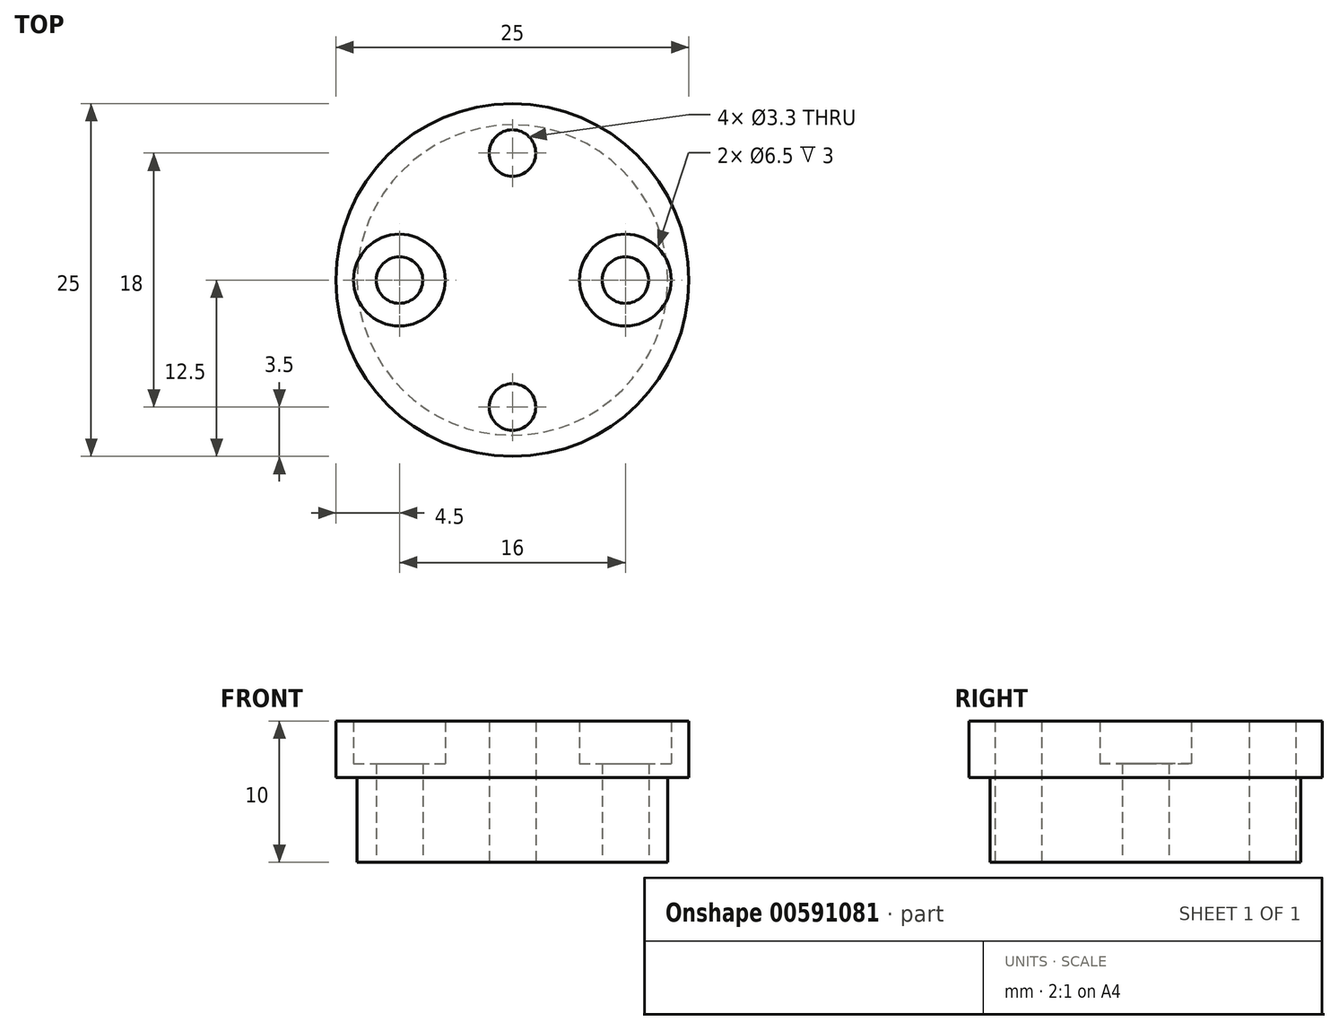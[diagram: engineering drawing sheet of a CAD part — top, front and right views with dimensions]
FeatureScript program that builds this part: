
annotation { "Feature Type Name" : "Feature", "Feature Type Description" : "" }
export const myFeature = defineFeature(function(context is Context, id is Id, definition is map)
    precondition{}
    {
        {
            var Q0;
            Q0=qCreatedBy(makeId("Front.planeOp"),FACE);
            var sketch = newSketch(context, id + "F0", { "sketchPlane" : qUnion([Q0])});
            skLineSegment(sketch, "E0", {"start": v(0, 0) * mm, "end": v(11, 0) * mm});
            skLineSegment(sketch, "E1", {"start": v(11, 0) * mm, "end": v(11, 6) * mm});
            skLineSegment(sketch, "E2", {"start": v(11, 6) * mm, "end": v(12.5, 6) * mm});
            skLineSegment(sketch, "E3", {"start": v(14, 10) * mm, "end": v(0, 10) * mm});
            skLineSegment(sketch, "E4", {"start": v(0, 10) * mm, "end": v(0, 0) * mm});
            skLineSegment(sketch, "E5", {"start": v(14, 10) * mm, "end": v(11, 0) * mm});
            skLineSegment(sketch, "E6", {"start": v(12.5, 10) * mm, "end": v(12.5, 6) * mm});
            skSolve(sketch);
        }
        {
            var Q0;
            Q0=makeQuery(id+"F0.imprint","IMPRINT",FACE,{"disambiguationData":[TD([[makeQuery(id+"F0.imprint","IMPRINT",EDGE,{"derivedFrom":sQuery(id+"F0.wireOp",EDGE,"E0")}),1.0]])]});
            var Q1;
            Q1=sQuery(id+"F0.wireOp",EDGE,"E4");
            revolve(context, id + "F1", {"entities" : qUnion([Q0]), "axis" : qUnion([Q1]), "revolveType" : RevolveType.FULL});
        }
        {
            var Q0;
            Q0=makeQuery(id+"F1.opRevolve","SWEPT_FACE",FACE,{"disambiguationData":[OSD([sQuery(id+"F0.wireOp",EDGE,"E3")])]});
            var sketch = newSketch(context, id + "F2", { "sketchPlane" : qUnion([Q0])});
            skLineSegment(sketch, "E7", {"start": v(-8, 0) * mm, "end": v(8, 0) * mm});
            skLineSegment(sketch, "E8", {"start": v(0, 9) * mm, "end": v(0, -9) * mm});
            skCircle(sketch, "E9.0", {"center": v(0, 0) * mm, "radius": 12.5 * mm});
            skSolve(sketch);
        }
        {
            var Q0;
            Q0=sQuery(id+"F2.wireOp",VERTEX,"E8.start");
            var Q1;
            Q1=sQuery(id+"F2.wireOp",VERTEX,"E8.end");
            var Q2;
            Q2=makeQuery(id+"F1.opRevolve","SWEPT_BODY",BODY,{"disambiguationData":[OSD([sQuery(id+"F0.wireOp",EDGE,"E0"),sQuery(id+"F0.wireOp",EDGE,"E1"),sQuery(id+"F0.wireOp",EDGE,"E2"),sQuery(id+"F0.wireOp",EDGE,"E3"),sQuery(id+"F0.wireOp",EDGE,"E4"),sQuery(id+"F0.wireOp",EDGE,"E6")])]});
            hole(context, id + "F3", {"style" : HoleStyle.SIMPLE, "endStyle" : HoleEndStyle.BLIND, "standardTappedOrClearance" : lookupTablePath({ "standard" : "ISO", "fit" : "Normal", "size" : "M3", "type" : "Clearance" }), "standardBlindInLast" : lookupTablePath({ "fit" : "Standard", "standard" : "ISO", "size" : "M3", "type" : "Clearance" }), "holeDiameter" : 3.3 * mm, "majorDiameter" : 5 * mm, "holeDepth" : 10 * mm, "isTappedThrough" : true, "tappedDepth" : 12 * mm, "tapClearance" : 3, "locations" : qUnion([Q0, Q1]), "scope" : qUnion([Q2])});
        }
        {
            var Q0;
            Q0=sQuery(id+"F2.wireOp",VERTEX,"E7.start");
            var Q1;
            Q1=sQuery(id+"F2.wireOp",VERTEX,"E7.end");
            var Q2;
            Q2=makeQuery(id+"F1.opRevolve","SWEPT_BODY",BODY,{"disambiguationData":[OSD([sQuery(id+"F0.wireOp",EDGE,"E0"),sQuery(id+"F0.wireOp",EDGE,"E1"),sQuery(id+"F0.wireOp",EDGE,"E2"),sQuery(id+"F0.wireOp",EDGE,"E3"),sQuery(id+"F0.wireOp",EDGE,"E4"),sQuery(id+"F0.wireOp",EDGE,"E6")])]});
            hole(context, id + "F4", {"style" : HoleStyle.C_BORE, "endStyle" : HoleEndStyle.BLIND, "standardTappedOrClearance" : lookupTablePath({ "standard" : "ISO", "fit" : "Normal", "size" : "M3", "type" : "Clearance" }), "standardBlindInLast" : lookupTablePath({ "fit" : "Standard", "standard" : "ISO", "size" : "M3", "type" : "Clearance" }), "holeDiameter" : 3.3 * mm, "cBoreDiameter" : 6.5 * mm, "cBoreDepth" : 3 * mm, "majorDiameter" : 5 * mm, "holeDepth" : 10 * mm, "isTappedThrough" : true, "tappedDepth" : 12 * mm, "tapClearance" : 3, "locations" : qUnion([Q0, Q1]), "scope" : qUnion([Q2])});
        }
    });
